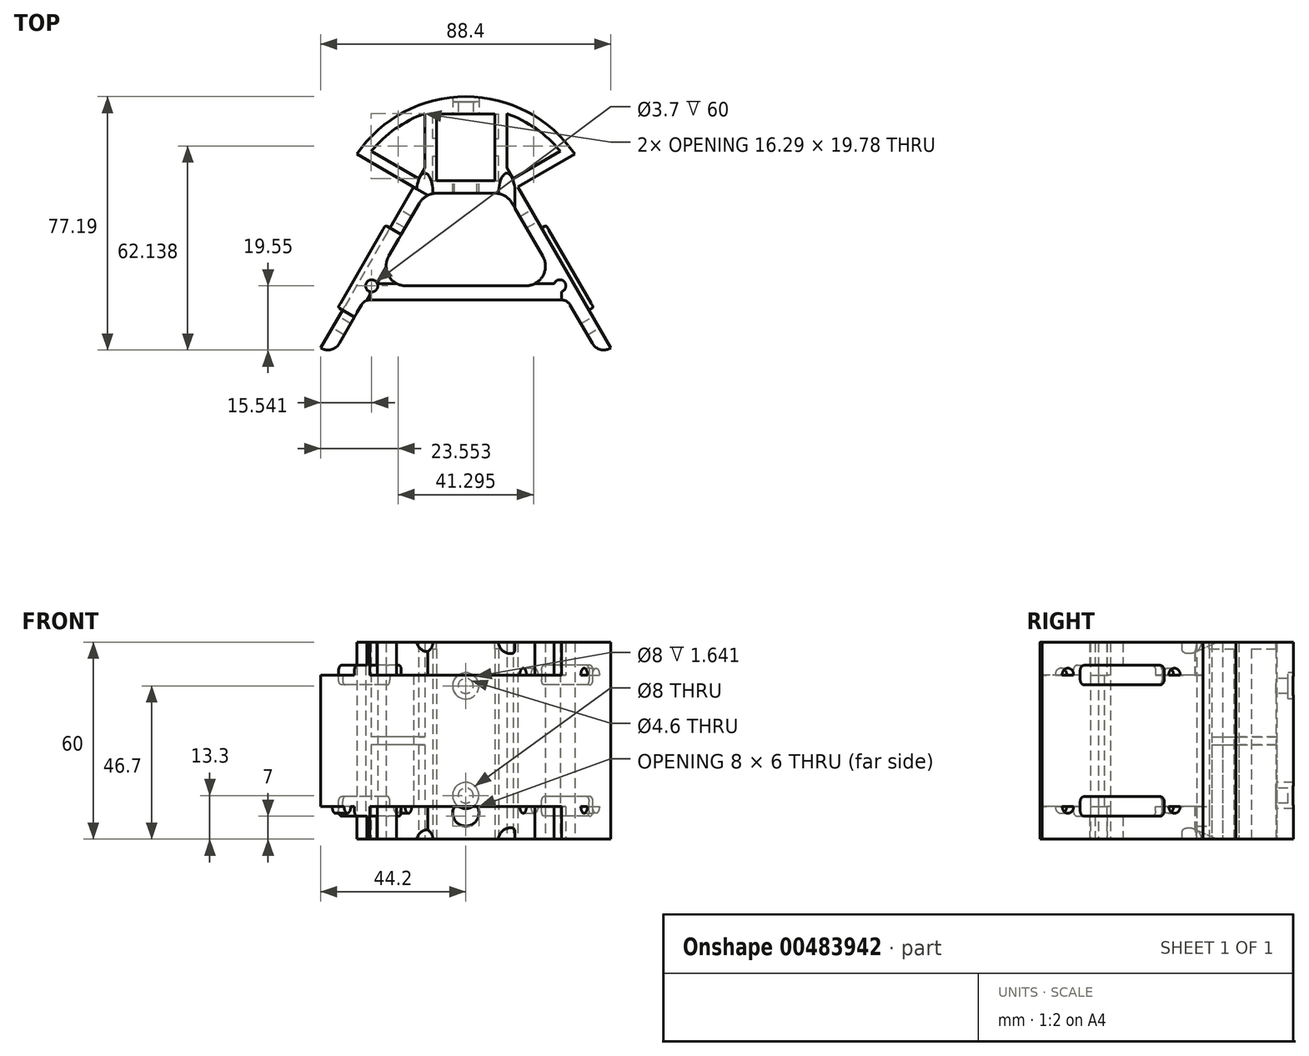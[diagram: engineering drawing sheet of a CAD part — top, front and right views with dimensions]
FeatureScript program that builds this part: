
annotation { "Feature Type Name" : "Feature", "Feature Type Description" : "" }
export const myFeature = defineFeature(function(context is Context, id is Id, definition is map)
    precondition{}
    {
        {
            var Q0;
            Q0=qCreatedBy(makeId("Top.planeOp"),FACE);
            var sketch = newSketch(context, id + "F0", { "sketchPlane" : qUnion([Q0])});
            skLineSegment(sketch, "E0", {"start": v(0, 0) * mm, "end": v(10, 0) * mm});
            skLineSegment(sketch, "E1", {"start": v(10, 0) * mm, "end": v(10, 7.5) * mm});
            skLineSegment(sketch, "E2", {"start": v(10, 7.5) * mm, "end": v(8.9, 7.5) * mm});
            skLineSegment(sketch, "E3", {"start": v(8.9, 7.5) * mm, "end": v(8.9, 12.8) * mm});
            skLineSegment(sketch, "E4", {"start": v(8.9, 12.8) * mm, "end": v(10, 12.8) * mm});
            skLineSegment(sketch, "E5", {"start": v(10, 12.8) * mm, "end": v(10, 20.3) * mm});
            skLineSegment(sketch, "E6", {"start": v(10, 20.3) * mm, "end": v(0, 20.3) * mm});
            skLineSegment(sketch, "E7", {"start": v(0, -3.8) * mm, "end": v(8.91, -3.8) * mm});
            skLineSegment(sketch, "E8", {"start": v(0, -32) * mm, "end": v(18.27, -32) * mm});
            skLineSegment(sketch, "E9", {"start": v(23.46, -23) * mm, "end": v(14.11, -6.8) * mm});
            skLineSegment(sketch, "E10", {"start": v(0, -36.3) * mm, "end": v(29.18, -36.3) * mm});
            skLineSegment(sketch, "E11", {"start": v(31.78, -37.8) * mm, "end": v(38.56, -49.55) * mm});
            skLineSegment(sketch, "E12", {"start": v(15.9, -1.9) * mm, "end": v(44.2, -50.92) * mm});
            skLineSegment(sketch, "E13", {"start": v(15.9, -1.9) * mm, "end": v(33.22, 8.1) * mm});
            skLineSegment(sketch, "E14", {"start": v(14.4, 0.7) * mm, "end": v(28.8, 9) * mm});
            skLineSegment(sketch, "E15", {"start": v(28.8, 9) * mm, "end": v(14.4, 0.7) * mm});
            skLineSegment(sketch, "E16", {"start": v(14.4, 0.7) * mm, "end": v(12.5, 3.99) * mm});
            skLineSegment(sketch, "E17", {"start": v(12.5, 3.99) * mm, "end": v(12.5, 20.48) * mm});
            skLineSegment(sketch, "E18", {"start": v(12.5, 3.99) * mm, "end": v(0, 25.64) * mm, "construction": true});
            skLineSegment(sketch, "E19", {"start": v(0, 25.64) * mm, "end": v(0, -14.6) * mm, "construction": true});
            skLineSegment(sketch, "E20", {"start": v(0, -14.6) * mm, "end": v(33.22, 8.1) * mm, "construction": true});
            skArc(sketch, "E21", {"start": v(0, 25.64) * mm, "mid": v(18.78, 20.99) * mm, "end": v(33.22, 8.1) * mm});
            skLineSegment(sketch, "E22", {"start": v(12.5, 20.48) * mm, "end": v(13.5, 23.3) * mm, "construction": true});
            skLineSegment(sketch, "E23", {"start": v(28.8, 9) * mm, "end": v(31.12, 10.91) * mm, "construction": true});
            skArc(sketch, "E24", {"start": v(28.8, 9) * mm, "mid": v(21.43, 15.85) * mm, "end": v(12.5, 20.48) * mm});
            skLineSegment(sketch, "E25", {"start": v(44.2, -50.92) * mm, "end": v(44.03, -51.02) * mm});
            skPoint(sketch, "E26.visualSharp", {"position": v(40.56, -53.02) * mm});
            skArc(sketch, "E26.filletArc", {"start": v(38.56, -49.55) * mm, "mid": v(41, -51.42) * mm, "end": v(44.03, -51.02) * mm});
            skPoint(sketch, "E27.visualSharp", {"position": v(30.91, -36.3) * mm});
            skArc(sketch, "E27.filletArc", {"start": v(31.78, -37.8) * mm, "mid": v(30.68, -36.7) * mm, "end": v(29.18, -36.3) * mm});
            skPoint(sketch, "E28.visualSharp", {"position": v(28.66, -32) * mm});
            skArc(sketch, "E28.filletArc", {"start": v(18.27, -32) * mm, "mid": v(23.46, -29) * mm, "end": v(23.46, -23) * mm});
            skPoint(sketch, "E29.visualSharp", {"position": v(12.38, -3.8) * mm});
            skArc(sketch, "E29.filletArc", {"start": v(14.11, -6.8) * mm, "mid": v(11.91, -4.6) * mm, "end": v(8.91, -3.8) * mm});
            skCircle(sketch, "E30", {"center": v(28.66, -32) * mm, "radius": 1.85 * mm});
            skLineSegment(sketch, "E31.MirrorCS", {"start": v(-44.2, -50.92) * mm, "end": v(-44.03, -51.02) * mm});
            skLineSegment(sketch, "E32.MirrorCS", {"start": v(-14.4, 0.7) * mm, "end": v(-12.5, 3.99) * mm});
            skLineSegment(sketch, "E33.MirrorCS", {"start": v(-10, 7.5) * mm, "end": v(-8.9, 7.5) * mm});
            skLineSegment(sketch, "E34.MirrorCS", {"start": v(-8.9, 12.8) * mm, "end": v(-10, 12.8) * mm});
            skLineSegment(sketch, "E35.MirrorCS", {"start": v(-28.8, 9) * mm, "end": v(-31.12, 10.91) * mm, "construction": true});
            skArc(sketch, "E36.MirrorCS", {"start": v(-31.78, -37.8) * mm, "mid": v(-30.68, -36.7) * mm, "end": v(-29.18, -36.3) * mm});
            skLineSegment(sketch, "E37.MirrorCS", {"start": v(-10, 0) * mm, "end": v(-10, 7.5) * mm});
            skArc(sketch, "E38.MirrorCS", {"start": v(-14.11, -6.8) * mm, "mid": v(-11.91, -4.6) * mm, "end": v(-8.91, -3.8) * mm});
            skLineSegment(sketch, "E39.MirrorCS", {"start": v(-12.5, 20.48) * mm, "end": v(-13.5, 23.3) * mm, "construction": true});
            skLineSegment(sketch, "E40.MirrorCS", {"start": v(-14.4, 0.7) * mm, "end": v(-28.8, 9) * mm});
            skLineSegment(sketch, "E41.MirrorCS", {"start": v(0, 0) * mm, "end": v(-10, 0) * mm});
            skArc(sketch, "E42.MirrorCS", {"start": v(-38.56, -49.55) * mm, "mid": v(-41, -51.42) * mm, "end": v(-44.03, -51.02) * mm});
            skCircle(sketch, "E43.MirrorC", {"center": v(-28.66, -32) * mm, "radius": 1.85 * mm});
            skLineSegment(sketch, "E44.MirrorCS", {"start": v(-8.9, 7.5) * mm, "end": v(-8.9, 12.8) * mm});
            skLineSegment(sketch, "E45.MirrorCS", {"start": v(-10, 12.8) * mm, "end": v(-10, 20.3) * mm});
            skLineSegment(sketch, "E46.MirrorCS", {"start": v(-12.5, 3.99) * mm, "end": v(0, 25.64) * mm, "construction": true});
            skLineSegment(sketch, "E47.MirrorCS", {"start": v(0, -14.6) * mm, "end": v(-33.22, 8.1) * mm, "construction": true});
            skPoint(sketch, "E48.MirrorP", {"position": v(-40.56, -53.02) * mm});
            skLineSegment(sketch, "E49.MirrorCS", {"start": v(-15.9, -1.9) * mm, "end": v(-44.2, -50.92) * mm});
            skLineSegment(sketch, "E50.MirrorCS", {"start": v(-31.78, -37.8) * mm, "end": v(-38.56, -49.55) * mm});
            skLineSegment(sketch, "E51.MirrorCS", {"start": v(-28.8, 9) * mm, "end": v(-14.4, 0.7) * mm});
            skLineSegment(sketch, "E52.MirrorCS", {"start": v(0, -36.3) * mm, "end": v(-29.18, -36.3) * mm});
            skLineSegment(sketch, "E53.MirrorCS", {"start": v(-23.46, -23) * mm, "end": v(-14.11, -6.8) * mm});
            skLineSegment(sketch, "E54.MirrorCS", {"start": v(-12.5, 3.99) * mm, "end": v(-12.5, 20.48) * mm});
            skLineSegment(sketch, "E55.MirrorCS", {"start": v(-15.9, -1.9) * mm, "end": v(-33.22, 8.1) * mm});
            skArc(sketch, "E56.MirrorCS", {"start": v(-18.27, -32) * mm, "mid": v(-23.46, -29) * mm, "end": v(-23.46, -23) * mm});
            skLineSegment(sketch, "E57.MirrorCS", {"start": v(0, -32) * mm, "end": v(-18.27, -32) * mm});
            skArc(sketch, "E58.MirrorCS", {"start": v(-28.8, 9) * mm, "mid": v(-21.43, 15.85) * mm, "end": v(-12.5, 20.48) * mm});
            skPoint(sketch, "E59.MirrorP", {"position": v(-12.38, -3.8) * mm});
            skLineSegment(sketch, "E60.MirrorCS", {"start": v(0, -3.8) * mm, "end": v(-8.91, -3.8) * mm});
            skLineSegment(sketch, "E61.MirrorCS", {"start": v(-10, 20.3) * mm, "end": v(0, 20.3) * mm});
            skPoint(sketch, "E62.MirrorP", {"position": v(-30.91, -36.3) * mm});
            skArc(sketch, "E63.MirrorCS", {"start": v(0, 25.64) * mm, "mid": v(-18.78, 20.99) * mm, "end": v(-33.22, 8.1) * mm});
            skSolve(sketch);
        }
        {
            var Q0;
            Q0=makeQuery(id+"F0.imprint","IMPRINT",FACE,{"disambiguationData":[TD([[makeQuery(id+"F0.imprint","IMPRINT",EDGE,{"derivedFrom":sQuery(id+"F0.wireOp",EDGE,"E0")}),-1.0]])]});
            extrude(context, id + "F1", {"entities" : qUnion([Q0]), "depth" : 30 * mm, "hasSecondDirection" : true, "secondDirectionOppositeDirection" : true, "secondDirectionDepth" : 30 * mm});
        }
        {
            var Q0;
            Q0=makeQuery(id+"F0.imprint","IMPRINT",FACE,{"disambiguationData":[TD([[makeQuery(id+"F0.imprint","IMPRINT",EDGE,{"derivedFrom":sQuery(id+"F0.wireOp",EDGE,"E32.MirrorCS")}),1.0]])]});
            var Q1;
            Q1=makeQuery(id+"F0.imprint","IMPRINT",FACE,{"disambiguationData":[TD([[makeQuery(id+"F0.imprint","IMPRINT",EDGE,{"derivedFrom":sQuery(id+"F0.wireOp",EDGE,"E15")}),-1.0]])]});
            extrude(context, id + "F2", {"entities" : qUnion([Q0, Q1]), "operationType" : NewBodyOperationType.ADD, "depth" : 1.2 * mm, "hasSecondDirection" : true, "secondDirectionOppositeDirection" : true, "secondDirectionDepth" : 1.2 * mm});
        }
        {
            var Q0;
            Q0=makeQuery(id+"F1.opExtrude","SWEPT_FACE",FACE,{"disambiguationData":[OSD([sQuery(id+"F0.wireOp",EDGE,"E0"),sQuery(id+"F0.wireOp",EDGE,"E41.MirrorCS")])]});
            var sketch = newSketch(context, id + "F3", { "sketchPlane" : qUnion([Q0])});
            skCircle(sketch, "E64", {"center": v(0, 0) * mm, "radius": 7 * mm});
            skCircle(sketch, "E65", {"center": v(0, -22) * mm, "radius": 4 * mm});
            skSolve(sketch);
        }
        {
            var Q0;
            Q0=makeQuery(id+"F3.imprint","IMPRINT",FACE,{"disambiguationData":[TD([[makeQuery(id+"F3.imprint","IMPRINT",EDGE,{"derivedFrom":sQuery(id+"F3.wireOp",EDGE,"E64")}),1.0]])]});
            var Q1;
            Q1=makeQuery(id+"F3.imprint","IMPRINT",FACE,{"disambiguationData":[TD([[makeQuery(id+"F3.imprint","IMPRINT",EDGE,{"derivedFrom":sQuery(id+"F3.wireOp",EDGE,"E65")}),1.0]])]});
            extrude(context, id + "F4", {"entities" : qUnion([Q0, Q1]), "operationType" : NewBodyOperationType.REMOVE, "oppositeDirection" : true, "depth" : 5 * mm});
        }
        {
            var Q0;
            Q0=makeQuery(id+"F1.opExtrude","SWEPT_FACE",FACE,{"disambiguationData":[OSD([sQuery(id+"F0.wireOp",EDGE,"E10"),sQuery(id+"F0.wireOp",EDGE,"E52.MirrorCS")])]});
            var sketch = newSketch(context, id + "F5", { "sketchPlane" : qUnion([Q0])});
            skCircle(sketch, "E66", {"center": v(0, 0) * mm, "radius": 11.8 * mm});
            skCircle(sketch, "E67", {"center": v(0, -22.5) * mm, "radius": 4.5 * mm});
            skCircle(sketch, "E68", {"center": v(15.4, 15.4) * mm, "radius": 1.6 * mm});
            skCircle(sketch, "E69.MirrorC", {"center": v(-15.4, 15.4) * mm, "radius": 1.6 * mm});
            skCircle(sketch, "E70.MirrorC", {"center": v(-15.4, -15.4) * mm, "radius": 1.6 * mm});
            skCircle(sketch, "E71.MirrorC", {"center": v(15.4, -15.4) * mm, "radius": 1.6 * mm});
            skSolve(sketch);
        }
        {
            var Q0;
            Q0=makeQuery(id+"F5.imprint","IMPRINT",FACE,{"disambiguationData":[TD([[makeQuery(id+"F5.imprint","IMPRINT",EDGE,{"derivedFrom":sQuery(id+"F5.wireOp",EDGE,"E66")}),1.0]])]});
            var Q1;
            Q1=makeQuery(id+"F5.imprint","IMPRINT",FACE,{"disambiguationData":[TD([[makeQuery(id+"F5.imprint","IMPRINT",EDGE,{"derivedFrom":sQuery(id+"F5.wireOp",EDGE,"E67")}),1.0]])]});
            var Q2;
            Q2=makeQuery(id+"F5.imprint","IMPRINT",FACE,{"disambiguationData":[TD([[makeQuery(id+"F5.imprint","IMPRINT",EDGE,{"derivedFrom":sQuery(id+"F5.wireOp",EDGE,"E71.MirrorC")}),-1.0]])]});
            var Q3;
            Q3=makeQuery(id+"F5.imprint","IMPRINT",FACE,{"disambiguationData":[TD([[makeQuery(id+"F5.imprint","IMPRINT",EDGE,{"derivedFrom":sQuery(id+"F5.wireOp",EDGE,"E68")}),1.0]])]});
            var Q4;
            Q4=makeQuery(id+"F5.imprint","IMPRINT",FACE,{"disambiguationData":[TD([[makeQuery(id+"F5.imprint","IMPRINT",EDGE,{"derivedFrom":sQuery(id+"F5.wireOp",EDGE,"E69.MirrorC")}),-1.0]])]});
            var Q5;
            Q5=makeQuery(id+"F5.imprint","IMPRINT",FACE,{"disambiguationData":[TD([[makeQuery(id+"F5.imprint","IMPRINT",EDGE,{"derivedFrom":sQuery(id+"F5.wireOp",EDGE,"E70.MirrorC")}),1.0]])]});
            extrude(context, id + "F6", {"entities" : qUnion([Q0, Q1, Q2, Q3, Q4, Q5]), "operationType" : NewBodyOperationType.REMOVE, "oppositeDirection" : true, "depth" : 5 * mm});
        }
        {
            var Q0;
            Q0=makeQuery(id+"F1.opExtrude","SWEPT_FACE",FACE,{"disambiguationData":[OSD([sQuery(id+"F0.wireOp",EDGE,"E12")])]});
            var sketch = newSketch(context, id + "F7", { "sketchPlane" : qUnion([Q0])});
            skCircle(sketch, "E72", {"center": v(-23.85, 0) * mm, "radius": 12.75 * mm});
            skLineSegment(sketch, "E73", {"start": v(-59.2, 7.25) * mm, "end": v(-59.2, -7.25) * mm});
            skLineSegment(sketch, "E74", {"start": v(-53.5, 7.25) * mm, "end": v(-53.5, -7.25) * mm});
            skArc(sketch, "E75", {"start": v(-53.5, 7.25) * mm, "mid": v(-56.35, 10.1) * mm, "end": v(-59.2, 7.25) * mm});
            skArc(sketch, "E76", {"start": v(-59.2, -7.25) * mm, "mid": v(-56.35, -10.1) * mm, "end": v(-53.5, -7.25) * mm});
            skCircle(sketch, "E77", {"center": v(-57.2, 20.1) * mm, "radius": 2 * mm});
            skPoint(sketch, "E77.centerSnap0", {"position": v(-56.35, 10.1) * mm});
            skCircle(sketch, "E78", {"center": v(-57.2, -20.1) * mm, "radius": 2 * mm});
            skCircle(sketch, "E79", {"center": v(-19.7, 20.1) * mm, "radius": 2 * mm});
            skCircle(sketch, "E80", {"center": v(-19.7, -20.1) * mm, "radius": 2 * mm});
            skLineSegment(sketch, "E81.bottom", {"start": v(-52.85, 23) * mm, "end": v(-24.05, 23) * mm});
            skLineSegment(sketch, "E81.top", {"start": v(-52.85, 17) * mm, "end": v(-24.05, 17) * mm});
            skLineSegment(sketch, "E81.left", {"start": v(-52.85, 23) * mm, "end": v(-52.85, 17) * mm});
            skLineSegment(sketch, "E81.right", {"start": v(-24.05, 23) * mm, "end": v(-24.05, 17) * mm});
            skLineSegment(sketch, "E82.MirrorCS", {"start": v(-52.85, -17) * mm, "end": v(-24.05, -17) * mm});
            skLineSegment(sketch, "E83.MirrorCS", {"start": v(-52.85, -23) * mm, "end": v(-52.85, -17) * mm});
            skLineSegment(sketch, "E84.MirrorCS", {"start": v(-52.85, -23) * mm, "end": v(-24.05, -23) * mm});
            skLineSegment(sketch, "E85.MirrorCS", {"start": v(-24.05, -23) * mm, "end": v(-24.05, -17) * mm});
            skSolve(sketch);
        }
        {
            var Q0;
            Q0=makeQuery(id+"F7.imprint","IMPRINT",FACE,{"disambiguationData":[TD([[makeQuery(id+"F7.imprint","IMPRINT",EDGE,{"derivedFrom":sQuery(id+"F7.wireOp",EDGE,"E73")}),1.0]])]});
            var Q1;
            Q1=makeQuery(id+"F7.imprint","IMPRINT",FACE,{"disambiguationData":[TD([[makeQuery(id+"F7.imprint","IMPRINT",EDGE,{"derivedFrom":sQuery(id+"F7.wireOp",EDGE,"E72")}),1.0]])]});
            var Q2;
            Q2=makeQuery(id+"F7.imprint","IMPRINT",FACE,{"disambiguationData":[TD([[makeQuery(id+"F7.imprint","IMPRINT",EDGE,{"derivedFrom":sQuery(id+"F7.wireOp",EDGE,"E79")}),1.0]])]});
            var Q3;
            Q3=makeQuery(id+"F7.imprint","IMPRINT",FACE,{"disambiguationData":[TD([[makeQuery(id+"F7.imprint","IMPRINT",EDGE,{"derivedFrom":sQuery(id+"F7.wireOp",EDGE,"E77")}),1.0]])]});
            var Q4;
            Q4=makeQuery(id+"F7.imprint","IMPRINT",FACE,{"disambiguationData":[TD([[makeQuery(id+"F7.imprint","IMPRINT",EDGE,{"derivedFrom":sQuery(id+"F7.wireOp",EDGE,"E78")}),1.0]])]});
            var Q5;
            Q5=makeQuery(id+"F7.imprint","IMPRINT",FACE,{"disambiguationData":[TD([[makeQuery(id+"F7.imprint","IMPRINT",EDGE,{"derivedFrom":sQuery(id+"F7.wireOp",EDGE,"E80")}),1.0]])]});
            extrude(context, id + "F8", {"entities" : qUnion([Q0, Q1, Q2, Q3, Q4, Q5]), "operationType" : NewBodyOperationType.REMOVE, "oppositeDirection" : true, "depth" : 5 * mm});
        }
        {
            var Q0;
            Q0=makeQuery(id+"F7.imprint","IMPRINT",FACE,{"disambiguationData":[TD([[makeQuery(id+"F7.imprint","IMPRINT",EDGE,{"derivedFrom":sQuery(id+"F7.wireOp",EDGE,"E81.bottom")}),-1.0]])]});
            var Q1;
            Q1=makeQuery(id+"F7.imprint","IMPRINT",FACE,{"disambiguationData":[TD([[makeQuery(id+"F7.imprint","IMPRINT",EDGE,{"derivedFrom":sQuery(id+"F7.wireOp",EDGE,"E82.MirrorCS")}),-1.0]])]});
            extrude(context, id + "F9", {"entities" : qUnion([Q0, Q1]), "operationType" : NewBodyOperationType.ADD, "depth" : 1.6 * mm});
        }
        {
            var Q0;
            Q0=makeQuery(id+"F1.opExtrude","SWEPT_FACE",FACE,{"disambiguationData":[OSD([sQuery(id+"F0.wireOp",EDGE,"E49.MirrorCS")])]});
            var sketch = newSketch(context, id + "F10", { "sketchPlane" : qUnion([Q0])});
            skCircle(sketch, "E86", {"center": v(23.85, 0) * mm, "radius": 12.75 * mm});
            skLineSegment(sketch, "E87", {"start": v(53.5, 7.25) * mm, "end": v(53.5, -7.25) * mm});
            skLineSegment(sketch, "E88", {"start": v(59.2, 7.25) * mm, "end": v(59.2, -7.25) * mm});
            skArc(sketch, "E89", {"start": v(59.2, 7.25) * mm, "mid": v(56.35, 10.1) * mm, "end": v(53.5, 7.25) * mm});
            skArc(sketch, "E90", {"start": v(53.5, -7.25) * mm, "mid": v(56.35, -10.1) * mm, "end": v(59.2, -7.25) * mm});
            skCircle(sketch, "E91", {"center": v(19.7, 20.1) * mm, "radius": 2 * mm});
            skPoint(sketch, "E91.centerSnap0", {"position": v(56.35, 10.1) * mm});
            skCircle(sketch, "E92", {"center": v(57.2, 20.1) * mm, "radius": 2 * mm});
            skLineSegment(sketch, "E93.bottom", {"start": v(24.05, 23) * mm, "end": v(52.85, 23) * mm});
            skLineSegment(sketch, "E93.top", {"start": v(24.05, 17) * mm, "end": v(52.85, 17) * mm});
            skLineSegment(sketch, "E93.left", {"start": v(24.05, 23) * mm, "end": v(24.05, 17) * mm});
            skLineSegment(sketch, "E93.right", {"start": v(52.85, 23) * mm, "end": v(52.85, 17) * mm});
            skLineSegment(sketch, "E94.MirrorCS", {"start": v(24.05, -23) * mm, "end": v(52.85, -23) * mm});
            skLineSegment(sketch, "E95.MirrorCS", {"start": v(52.85, -23) * mm, "end": v(52.85, -17) * mm});
            skLineSegment(sketch, "E96.MirrorCS", {"start": v(24.05, -23) * mm, "end": v(24.05, -17) * mm});
            skLineSegment(sketch, "E97.MirrorCS", {"start": v(24.05, -17) * mm, "end": v(52.85, -17) * mm});
            skCircle(sketch, "E98.MirrorC", {"center": v(57.2, -20.1) * mm, "radius": 2 * mm});
            skCircle(sketch, "E99.MirrorC", {"center": v(19.7, -20.1) * mm, "radius": 2 * mm});
            skSolve(sketch);
        }
        {
            var Q0;
            Q0=makeQuery(id+"F10.imprint","IMPRINT",FACE,{"disambiguationData":[TD([[makeQuery(id+"F10.imprint","IMPRINT",EDGE,{"derivedFrom":sQuery(id+"F10.wireOp",EDGE,"E86")}),1.0]])]});
            var Q1;
            Q1=makeQuery(id+"F10.imprint","IMPRINT",FACE,{"disambiguationData":[TD([[makeQuery(id+"F10.imprint","IMPRINT",EDGE,{"derivedFrom":sQuery(id+"F10.wireOp",EDGE,"E87")}),1.0]])]});
            var Q2;
            Q2=makeQuery(id+"F10.imprint","IMPRINT",FACE,{"disambiguationData":[TD([[makeQuery(id+"F10.imprint","IMPRINT",EDGE,{"derivedFrom":sQuery(id+"F10.wireOp",EDGE,"E98.MirrorC")}),-1.0]])]});
            var Q3;
            Q3=makeQuery(id+"F10.imprint","IMPRINT",FACE,{"disambiguationData":[TD([[makeQuery(id+"F10.imprint","IMPRINT",EDGE,{"derivedFrom":sQuery(id+"F10.wireOp",EDGE,"E91")}),1.0]])]});
            var Q4;
            Q4=makeQuery(id+"F10.imprint","IMPRINT",FACE,{"disambiguationData":[TD([[makeQuery(id+"F10.imprint","IMPRINT",EDGE,{"derivedFrom":sQuery(id+"F10.wireOp",EDGE,"E92")}),1.0]])]});
            var Q5;
            Q5=makeQuery(id+"F10.imprint","IMPRINT",FACE,{"disambiguationData":[TD([[makeQuery(id+"F10.imprint","IMPRINT",EDGE,{"derivedFrom":sQuery(id+"F10.wireOp",EDGE,"E99.MirrorC")}),-1.0]])]});
            extrude(context, id + "F11", {"entities" : qUnion([Q0, Q1, Q2, Q3, Q4, Q5]), "operationType" : NewBodyOperationType.REMOVE, "oppositeDirection" : true, "depth" : 5 * mm});
        }
        {
            var Q0;
            Q0=makeQuery(id+"F10.imprint","IMPRINT",FACE,{"disambiguationData":[TD([[makeQuery(id+"F10.imprint","IMPRINT",EDGE,{"derivedFrom":sQuery(id+"F10.wireOp",EDGE,"E93.bottom")}),-1.0]])]});
            var Q1;
            Q1=makeQuery(id+"F10.imprint","IMPRINT",FACE,{"disambiguationData":[TD([[makeQuery(id+"F10.imprint","IMPRINT",EDGE,{"derivedFrom":sQuery(id+"F10.wireOp",EDGE,"E94.MirrorCS")}),1.0]])]});
            extrude(context, id + "F12", {"entities" : qUnion([Q0, Q1]), "operationType" : NewBodyOperationType.ADD, "depth" : 1.6 * mm});
        }
        {
            var Q0;
            Q0=makeQuery(id+"F0.imprint","IMPRINT",FACE,{"disambiguationData":[TD([[makeQuery(id+"F0.imprint","IMPRINT",EDGE,{"derivedFrom":sQuery(id+"F0.wireOp",EDGE,"E43.MirrorC")}),-1.0]])]});
            var Q1;
            Q1=makeQuery(id+"F0.imprint","IMPRINT",FACE,{"disambiguationData":[TD([[makeQuery(id+"F0.imprint","IMPRINT",EDGE,{"derivedFrom":sQuery(id+"F0.wireOp",EDGE,"E30")}),1.0]])]});
            extrude(context, id + "F13", {"entities" : qUnion([Q0, Q1]), "operationType" : NewBodyOperationType.ADD, "depth" : 20 * mm, "hasSecondDirection" : true, "secondDirectionOppositeDirection" : true, "secondDirectionDepth" : 20 * mm});
        }
        {
            var Q0;
            Q0=makeQuery(id+"F1.opExtrude","SWEPT_FACE",FACE,{"disambiguationData":[OSD([sQuery(id+"F0.wireOp",EDGE,"E6"),sQuery(id+"F0.wireOp",EDGE,"E61.MirrorCS")])]});
            var sketch = newSketch(context, id + "F14", { "sketchPlane" : qUnion([Q0])});
            skCircle(sketch, "E100", {"center": v(0, 16.7) * mm, "radius": 2.3 * mm});
            skCircle(sketch, "E101.MirrorC", {"center": v(0, -16.7) * mm, "radius": 2.3 * mm});
            skCircle(sketch, "E102", {"center": v(0, -16.7) * mm, "radius": 4 * mm});
            skCircle(sketch, "E103", {"center": v(0, 16.7) * mm, "radius": 4 * mm});
            skSolve(sketch);
        }
        {
            var Q0;
            Q0=makeQuery(id+"F14.imprint","IMPRINT",FACE,{"disambiguationData":[TD([[makeQuery(id+"F14.imprint","IMPRINT",EDGE,{"derivedFrom":sQuery(id+"F14.wireOp",EDGE,"E101.MirrorC")}),-1.0]])]});
            var Q1;
            Q1=makeQuery(id+"F14.imprint","IMPRINT",FACE,{"disambiguationData":[TD([[makeQuery(id+"F14.imprint","IMPRINT",EDGE,{"derivedFrom":sQuery(id+"F14.wireOp",EDGE,"E100")}),1.0]])]});
            extrude(context, id + "F15", {"entities" : qUnion([Q0, Q1]), "operationType" : NewBodyOperationType.REMOVE, "oppositeDirection" : true, "depth" : 8 * mm});
        }
        {
            var Q0;
            Q0=makeQuery(id+"F14.imprint","IMPRINT",FACE,{"disambiguationData":[TD([[makeQuery(id+"F14.imprint","IMPRINT",EDGE,{"derivedFrom":sQuery(id+"F14.wireOp",EDGE,"E101.MirrorC")}),1.0]])]});
            var Q1;
            Q1=makeQuery(id+"F14.imprint","IMPRINT",FACE,{"disambiguationData":[TD([[makeQuery(id+"F14.imprint","IMPRINT",EDGE,{"derivedFrom":sQuery(id+"F14.wireOp",EDGE,"E100")}),-1.0]])]});
            extrude(context, id + "F16", {"entities" : qUnion([Q0, Q1]), "operationType" : NewBodyOperationType.REMOVE, "oppositeDirection" : true, "depth" : 6 * mm});
        }
        {
            var Q0;
            Q0=makeQuery(id+"F14.imprint","IMPRINT",FACE,{"disambiguationData":[TD([[makeQuery(id+"F14.imprint","IMPRINT",EDGE,{"derivedFrom":sQuery(id+"F14.wireOp",EDGE,"E101.MirrorC")}),1.0]])]});
            var Q1;
            Q1=makeQuery(id+"F14.imprint","IMPRINT",FACE,{"disambiguationData":[TD([[makeQuery(id+"F14.imprint","IMPRINT",EDGE,{"derivedFrom":sQuery(id+"F14.wireOp",EDGE,"E100")}),-1.0]])]});
            extrude(context, id + "F17", {"entities" : qUnion([Q0, Q1]), "operationType" : NewBodyOperationType.ADD, "oppositeDirection" : true, "depth" : 3.7 * mm});
        }
        {
            var Q0;
            Q0=makeQuery(id+"F1.opExtrude","CAP_EDGE",EDGE,{"disambiguationData":[OSD([sQuery(id+"F0.wireOp",EDGE,"E7"),sQuery(id+"F0.wireOp",EDGE,"E60.MirrorCS")])],"isStart":true});
            cPoint(context, id + "F18", {"entities" : qUnion([Q0]), "parameter" : 0.5});
        }
        {
            var Q0;
            Q0=sQuery(id+"F5.wireOp",VERTEX,"E71.MirrorC.center");
            var Q1;
            Q1=sQuery(id+"F5.wireOp",VERTEX,"E70.MirrorC.center");
            var Q2;
            Q2 = qCreatedBy(id + "F18" ,VERTEX);
            cPlane(context, id + "F19", {"entities" : qUnion([Q0, Q1, Q2]), "cplaneType" : CPlaneType.THREE_POINT, "offset" : 25 * mm, "flipAlignment" : true, "width" : 150 * mm, "height" : 150 * mm});
        }
        {
            var Q0;
            Q0=qCreatedBy(id+"F19.planeOp",FACE);
            var sketch = newSketch(context, id + "F20", { "sketchPlane" : qUnion([Q0])});
            skLineSegment(sketch, "E104.bottom", {"start": v(-8.91, 8.83) * mm, "end": v(8.91, 8.83) * mm});
            skLineSegment(sketch, "E104.top", {"start": v(-8.91, 3.83) * mm, "end": v(8.91, 3.83) * mm});
            skLineSegment(sketch, "E104.left", {"start": v(-8.91, 8.83) * mm, "end": v(-8.91, 3.83) * mm});
            skLineSegment(sketch, "E104.right", {"start": v(8.91, 8.83) * mm, "end": v(8.91, 3.83) * mm});
            skSolve(sketch);
        }
        {
            var Q0;
            Q0=makeQuery(id+"F20.imprint","IMPRINT",FACE,{"disambiguationData":[TD([[makeQuery(id+"F20.imprint","IMPRINT",EDGE,{"derivedFrom":sQuery(id+"F20.wireOp",EDGE,"E104.bottom")}),-1.0]])]});
            extrude(context, id + "F21", {"entities" : qUnion([Q0]), "oppositeDirection" : true, "depth" : 20 * mm});
        }
        {
            var Q0;
            Q0=makeQuery(id+"F21.opExtrude","SWEPT_FACE",FACE,{"disambiguationData":[OSD([sQuery(id+"F20.wireOp",EDGE,"E104.bottom")])]});
            var sketch = newSketch(context, id + "F22", { "sketchPlane" : qUnion([Q0])});
            skCircle(sketch, "E105", {"center": v(-12.5, -28.92) * mm, "radius": 2.5 * mm});
            skCircle(sketch, "E106", {"center": v(12.5, -28.92) * mm, "radius": 2.5 * mm});
            skLineSegment(sketch, "E107.bottom", {"start": v(15, -28.92) * mm, "end": v(10, -28.92) * mm});
            skLineSegment(sketch, "E107.top", {"start": v(15, -35.42) * mm, "end": v(10, -35.42) * mm});
            skLineSegment(sketch, "E107.left", {"start": v(15, -28.92) * mm, "end": v(15, -35.42) * mm});
            skLineSegment(sketch, "E107.right", {"start": v(10, -28.92) * mm, "end": v(10, -35.42) * mm});
            skLineSegment(sketch, "E108.bottom", {"start": v(-15, -28.92) * mm, "end": v(-10, -28.92) * mm});
            skLineSegment(sketch, "E108.top", {"start": v(-15, -35.42) * mm, "end": v(-10, -35.42) * mm});
            skLineSegment(sketch, "E108.left", {"start": v(-15, -28.92) * mm, "end": v(-15, -35.42) * mm});
            skLineSegment(sketch, "E108.right", {"start": v(-10, -28.92) * mm, "end": v(-10, -35.42) * mm});
            skSolve(sketch);
        }
        {
            var Q0;
            {var subQ0=sQuery(id+"F22.wireOp",EDGE,"E107.bottom");Q0=makeQuery(id+"F22.imprint","IMPRINT",FACE,{"disambiguationData":[TD([[makeQuery(id+"F22.imprint","IMPRINT",EDGE,{"derivedFrom":subQ0}),1.0]])]});}
            var Q1;
            Q1=makeQuery(id+"F22.imprint","IMPRINT",FACE,{"disambiguationData":[TD([[makeQuery(id+"F22.imprint","IMPRINT",EDGE,{"derivedFrom":sQuery(id+"F22.wireOp",EDGE,"E107.top")}),-1.0]])]});
            var Q2;
            Q2=makeQuery(id+"F22.imprint","IMPRINT",FACE,{"disambiguationData":[TD([[makeQuery(id+"F22.imprint","IMPRINT",EDGE,{"derivedFrom":sQuery(id+"F22.wireOp",EDGE,"E108.top")}),1.0]])]});
            var Q3;
            {var subQ0=sQuery(id+"F22.wireOp",EDGE,"E108.bottom");Q3=makeQuery(id+"F22.imprint","IMPRINT",FACE,{"disambiguationData":[TD([[makeQuery(id+"F22.imprint","IMPRINT",EDGE,{"derivedFrom":subQ0}),-1.0]])]});}
            var Q4;
            {var subQ0=sQuery(id+"F22.wireOp",EDGE,"E107.bottom");Q4=makeQuery(id+"F22.imprint","IMPRINT",FACE,{"disambiguationData":[TD([[makeQuery(id+"F22.imprint","IMPRINT",EDGE,{"derivedFrom":subQ0}),-1.0]])]});}
            var Q5;
            {var subQ0=sQuery(id+"F22.wireOp",EDGE,"E108.bottom");Q5=makeQuery(id+"F22.imprint","IMPRINT",FACE,{"disambiguationData":[TD([[makeQuery(id+"F22.imprint","IMPRINT",EDGE,{"derivedFrom":subQ0}),1.0]])]});}
            extrude(context, id + "F23", {"entities" : qUnion([Q0, Q1, Q2, Q3, Q4, Q5]), "oppositeDirection" : true, "depth" : 10 * mm, "hasSecondDirection" : true, "secondDirectionOppositeDirection" : false, "secondDirectionDepth" : 10 * mm});
        }
        {
            var Q0;
            Q0=makeQuery(id+"F1.opExtrude","CAP_FACE",FACE,{"disambiguationData":[OSD([sQuery(id+"F0.wireOp",EDGE,"E0"),sQuery(id+"F0.wireOp",EDGE,"E1"),sQuery(id+"F0.wireOp",EDGE,"E2"),sQuery(id+"F0.wireOp",EDGE,"E3"),sQuery(id+"F0.wireOp",EDGE,"E4"),sQuery(id+"F0.wireOp",EDGE,"E5"),sQuery(id+"F0.wireOp",EDGE,"E6"),sQuery(id+"F0.wireOp",EDGE,"E7"),sQuery(id+"F0.wireOp",EDGE,"E8"),sQuery(id+"F0.wireOp",EDGE,"E9"),sQuery(id+"F0.wireOp",EDGE,"E10"),sQuery(id+"F0.wireOp",EDGE,"E11"),sQuery(id+"F0.wireOp",EDGE,"E12"),sQuery(id+"F0.wireOp",EDGE,"E13"),sQuery(id+"F0.wireOp",EDGE,"E15"),sQuery(id+"F0.wireOp",EDGE,"E16"),sQuery(id+"F0.wireOp",EDGE,"E17"),sQuery(id+"F0.wireOp",EDGE,"E21"),sQuery(id+"F0.wireOp",EDGE,"E24"),sQuery(id+"F0.wireOp",EDGE,"E25"),sQuery(id+"F0.wireOp",EDGE,"E26.filletArc"),sQuery(id+"F0.wireOp",EDGE,"E27.filletArc"),sQuery(id+"F0.wireOp",EDGE,"E28.filletArc"),sQuery(id+"F0.wireOp",EDGE,"E29.filletArc"),sQuery(id+"F0.wireOp",EDGE,"E30"),sQuery(id+"F0.wireOp",EDGE,"E31.MirrorCS"),sQuery(id+"F0.wireOp",EDGE,"E32.MirrorCS"),sQuery(id+"F0.wireOp",EDGE,"E33.MirrorCS"),sQuery(id+"F0.wireOp",EDGE,"E34.MirrorCS"),sQuery(id+"F0.wireOp",EDGE,"E36.MirrorCS"),sQuery(id+"F0.wireOp",EDGE,"E37.MirrorCS"),sQuery(id+"F0.wireOp",EDGE,"E38.MirrorCS"),sQuery(id+"F0.wireOp",EDGE,"E41.MirrorCS"),sQuery(id+"F0.wireOp",EDGE,"E42.MirrorCS"),sQuery(id+"F0.wireOp",EDGE,"E43.MirrorC"),sQuery(id+"F0.wireOp",EDGE,"E44.MirrorCS"),sQuery(id+"F0.wireOp",EDGE,"E45.MirrorCS"),sQuery(id+"F0.wireOp",EDGE,"E49.MirrorCS"),sQuery(id+"F0.wireOp",EDGE,"E50.MirrorCS"),sQuery(id+"F0.wireOp",EDGE,"E51.MirrorCS"),sQuery(id+"F0.wireOp",EDGE,"E52.MirrorCS"),sQuery(id+"F0.wireOp",EDGE,"E53.MirrorCS"),sQuery(id+"F0.wireOp",EDGE,"E54.MirrorCS"),sQuery(id+"F0.wireOp",EDGE,"E55.MirrorCS"),sQuery(id+"F0.wireOp",EDGE,"E56.MirrorCS"),sQuery(id+"F0.wireOp",EDGE,"E57.MirrorCS"),sQuery(id+"F0.wireOp",EDGE,"E58.MirrorCS"),sQuery(id+"F0.wireOp",EDGE,"E60.MirrorCS"),sQuery(id+"F0.wireOp",EDGE,"E61.MirrorCS"),sQuery(id+"F0.wireOp",EDGE,"E63.MirrorCS")])],"isStart":false});
            var sketch = newSketch(context, id + "F24", { "sketchPlane" : qUnion([Q0])});
            skLineSegment(sketch, "E109", {"start": v(-8.9, 12.8) * mm, "end": v(-8.9, 20.3) * mm});
            skLineSegment(sketch, "E110", {"start": v(-8.9, 20.3) * mm, "end": v(-10, 20.3) * mm});
            skLineSegment(sketch, "E111", {"start": v(-10, 20.3) * mm, "end": v(-10, 0) * mm});
            skLineSegment(sketch, "E112", {"start": v(-10, 0) * mm, "end": v(-8.9, 0) * mm});
            skLineSegment(sketch, "E113", {"start": v(-8.9, 0) * mm, "end": v(-8.9, 12.8) * mm});
            skLineSegment(sketch, "E114", {"start": v(10, 20.3) * mm, "end": v(10, 0) * mm});
            skLineSegment(sketch, "E115", {"start": v(10, 0) * mm, "end": v(8.9, 0) * mm});
            skLineSegment(sketch, "E116", {"start": v(8.9, 0) * mm, "end": v(8.9, 20.3) * mm});
            skLineSegment(sketch, "E117", {"start": v(8.9, 20.3) * mm, "end": v(10, 20.3) * mm});
            skSolve(sketch);
        }
        {
            var Q0;
            Q0=makeQuery(id+"F24.imprint","IMPRINT",FACE,{"disambiguationData":[TD([[makeQuery(id+"F24.imprint","IMPRINT",EDGE,{"derivedFrom":sQuery(id+"F24.wireOp",EDGE,"E109")}),1.0]])]});
            var Q1;
            {var subQ2=sQuery(id+"F24.wireOp",EDGE,"E112");Q1=makeQuery(id+"F24.imprint","IMPRINT",FACE,{"disambiguationData":[TD([[makeQuery(id+"F24.imprint","IMPRINT",EDGE,{"derivedFrom":subQ2}),1.0]])]});}
            var Q2;
            {var subQ2=sQuery(id+"F24.wireOp",EDGE,"E117");Q2=makeQuery(id+"F24.imprint","IMPRINT",FACE,{"disambiguationData":[TD([[makeQuery(id+"F24.imprint","IMPRINT",EDGE,{"derivedFrom":subQ2}),-1.0]])]});}
            var Q3;
            {var subQ0=sQuery(id+"F24.wireOp",EDGE,"E115");Q3=makeQuery(id+"F24.imprint","IMPRINT",FACE,{"disambiguationData":[TD([[makeQuery(id+"F24.imprint","IMPRINT",EDGE,{"derivedFrom":subQ0}),1.0]])]});}
            extrude(context, id + "F25", {"entities" : qUnion([Q0, Q1, Q2, Q3]), "operationType" : NewBodyOperationType.ADD, "oppositeDirection" : true, "depth" : 2 * mm});
        }
        {
            var Q0;
            Q0=makeQuery(id+"F9.opExtrude","SWEPT_EDGE",EDGE,{"disambiguationData":[OSD([sQuery(id+"F7.wireOp",EDGE,"E81.bottom"),sQuery(id+"F7.wireOp",EDGE,"E81.left")])]});
            var Q1;
            Q1=makeQuery(id+"F9.opExtrude","SWEPT_EDGE",EDGE,{"disambiguationData":[OSD([sQuery(id+"F7.wireOp",EDGE,"E81.top"),sQuery(id+"F7.wireOp",EDGE,"E81.left")])]});
            var Q2;
            Q2=makeQuery(id+"F9.opExtrude","SWEPT_EDGE",EDGE,{"disambiguationData":[OSD([sQuery(id+"F7.wireOp",EDGE,"E81.bottom"),sQuery(id+"F7.wireOp",EDGE,"E81.right")])]});
            var Q3;
            Q3=makeQuery(id+"F9.opExtrude","SWEPT_EDGE",EDGE,{"disambiguationData":[OSD([sQuery(id+"F7.wireOp",EDGE,"E81.top"),sQuery(id+"F7.wireOp",EDGE,"E81.right")])]});
            var Q4;
            Q4=makeQuery(id+"F9.opExtrude","SWEPT_EDGE",EDGE,{"disambiguationData":[OSD([sQuery(id+"F7.wireOp",EDGE,"E82.MirrorCS"),sQuery(id+"F7.wireOp",EDGE,"E85.MirrorCS")])]});
            var Q5;
            Q5=makeQuery(id+"F9.opExtrude","SWEPT_EDGE",EDGE,{"disambiguationData":[OSD([sQuery(id+"F7.wireOp",EDGE,"E84.MirrorCS"),sQuery(id+"F7.wireOp",EDGE,"E85.MirrorCS")])]});
            var Q6;
            Q6=makeQuery(id+"F9.opExtrude","SWEPT_EDGE",EDGE,{"disambiguationData":[OSD([sQuery(id+"F7.wireOp",EDGE,"E82.MirrorCS"),sQuery(id+"F7.wireOp",EDGE,"E83.MirrorCS")])]});
            var Q7;
            Q7=makeQuery(id+"F9.opExtrude","SWEPT_EDGE",EDGE,{"disambiguationData":[OSD([sQuery(id+"F7.wireOp",EDGE,"E83.MirrorCS"),sQuery(id+"F7.wireOp",EDGE,"E84.MirrorCS")])]});
            var Q8;
            Q8=makeQuery(id+"F12.opExtrude","SWEPT_EDGE",EDGE,{"disambiguationData":[OSD([sQuery(id+"F10.wireOp",EDGE,"E93.bottom"),sQuery(id+"F10.wireOp",EDGE,"E93.right")])]});
            var Q9;
            Q9=makeQuery(id+"F12.opExtrude","SWEPT_EDGE",EDGE,{"disambiguationData":[OSD([sQuery(id+"F10.wireOp",EDGE,"E93.top"),sQuery(id+"F10.wireOp",EDGE,"E93.right")])]});
            var Q10;
            Q10=makeQuery(id+"F12.opExtrude","SWEPT_EDGE",EDGE,{"disambiguationData":[OSD([sQuery(id+"F10.wireOp",EDGE,"E95.MirrorCS"),sQuery(id+"F10.wireOp",EDGE,"E97.MirrorCS")])]});
            var Q11;
            Q11=makeQuery(id+"F12.opExtrude","SWEPT_EDGE",EDGE,{"disambiguationData":[OSD([sQuery(id+"F10.wireOp",EDGE,"E94.MirrorCS"),sQuery(id+"F10.wireOp",EDGE,"E95.MirrorCS")])]});
            var Q12;
            Q12=makeQuery(id+"F12.opExtrude","SWEPT_EDGE",EDGE,{"disambiguationData":[OSD([sQuery(id+"F10.wireOp",EDGE,"E93.bottom"),sQuery(id+"F10.wireOp",EDGE,"E93.left")])]});
            var Q13;
            Q13=makeQuery(id+"F12.opExtrude","SWEPT_EDGE",EDGE,{"disambiguationData":[OSD([sQuery(id+"F10.wireOp",EDGE,"E93.top"),sQuery(id+"F10.wireOp",EDGE,"E93.left")])]});
            var Q14;
            Q14=makeQuery(id+"F12.opExtrude","SWEPT_EDGE",EDGE,{"disambiguationData":[OSD([sQuery(id+"F10.wireOp",EDGE,"E96.MirrorCS"),sQuery(id+"F10.wireOp",EDGE,"E97.MirrorCS")])]});
            var Q15;
            Q15=makeQuery(id+"F12.opExtrude","SWEPT_EDGE",EDGE,{"disambiguationData":[OSD([sQuery(id+"F10.wireOp",EDGE,"E94.MirrorCS"),sQuery(id+"F10.wireOp",EDGE,"E96.MirrorCS")])]});
            fillet(context, id + "F26", {"entities" : qUnion([Q0, Q1, Q2, Q3, Q4, Q5, Q6, Q7, Q8, Q9, Q10, Q11, Q12, Q13, Q14, Q15]), "radius" : 1.5 * mm, "tangentPropagation" : true, "allowEdgeOverflow" : false});
        }
        {
            var Q0;
            Q0=makeQuery(id+"F12.opExtrude","CAP_FACE",FACE,{"disambiguationData":[OSD([sQuery(id+"F10.wireOp",EDGE,"E93.bottom"),sQuery(id+"F10.wireOp",EDGE,"E93.top"),sQuery(id+"F10.wireOp",EDGE,"E93.left"),sQuery(id+"F10.wireOp",EDGE,"E93.right")])],"isStart":false});
            var Q1;
            Q1=makeQuery(id+"F12.opExtrude","CAP_FACE",FACE,{"disambiguationData":[OSD([sQuery(id+"F10.wireOp",EDGE,"E94.MirrorCS"),sQuery(id+"F10.wireOp",EDGE,"E95.MirrorCS"),sQuery(id+"F10.wireOp",EDGE,"E96.MirrorCS"),sQuery(id+"F10.wireOp",EDGE,"E97.MirrorCS")])],"isStart":false});
            var Q2;
            Q2=makeQuery(id+"F9.opExtrude","CAP_FACE",FACE,{"disambiguationData":[OSD([sQuery(id+"F7.wireOp",EDGE,"E81.bottom"),sQuery(id+"F7.wireOp",EDGE,"E81.top"),sQuery(id+"F7.wireOp",EDGE,"E81.left"),sQuery(id+"F7.wireOp",EDGE,"E81.right")])],"isStart":false});
            var Q3;
            Q3=makeQuery(id+"F9.opExtrude","CAP_FACE",FACE,{"disambiguationData":[OSD([sQuery(id+"F7.wireOp",EDGE,"E82.MirrorCS"),sQuery(id+"F7.wireOp",EDGE,"E83.MirrorCS"),sQuery(id+"F7.wireOp",EDGE,"E84.MirrorCS"),sQuery(id+"F7.wireOp",EDGE,"E85.MirrorCS")])],"isStart":false});
            fillet(context, id + "F27", {"entities" : qUnion([Q0, Q1, Q2, Q3]), "radius" : 0.5 * mm, "tangentPropagation" : true, "allowEdgeOverflow" : false});
        }
        {
            var Q0;
            Q0=makeQuery(id+"F23.opExtrude","SWEPT_BODY",BODY,{"disambiguationData":[OSD([sQuery(id+"F22.wireOp",EDGE,"E105"),sQuery(id+"F22.wireOp",EDGE,"E108.top"),sQuery(id+"F22.wireOp",EDGE,"E108.left"),sQuery(id+"F22.wireOp",EDGE,"E108.right")])]});
            var Q1;
            Q1=makeQuery(id+"F23.opExtrude","SWEPT_BODY",BODY,{"disambiguationData":[OSD([sQuery(id+"F22.wireOp",EDGE,"E106"),sQuery(id+"F22.wireOp",EDGE,"E107.top"),sQuery(id+"F22.wireOp",EDGE,"E107.left"),sQuery(id+"F22.wireOp",EDGE,"E107.right")])]});
            var Q2;
            Q2=qCreatedBy(makeId("Top.planeOp"),FACE);
            mirror(context, id + "F28", {"entities" : qUnion([Q0, Q1]), "mirrorPlane" : qUnion([Q2])});
        }
        {
            var Q0;
            Q0=makeQuery(id+"F23.opExtrude","SWEPT_BODY",BODY,{"disambiguationData":[OSD([sQuery(id+"F22.wireOp",EDGE,"E105"),sQuery(id+"F22.wireOp",EDGE,"E108.top"),sQuery(id+"F22.wireOp",EDGE,"E108.left"),sQuery(id+"F22.wireOp",EDGE,"E108.right")])]});
            var Q1;
            Q1=makeQuery(id+"F23.opExtrude","SWEPT_BODY",BODY,{"disambiguationData":[OSD([sQuery(id+"F22.wireOp",EDGE,"E106"),sQuery(id+"F22.wireOp",EDGE,"E107.top"),sQuery(id+"F22.wireOp",EDGE,"E107.left"),sQuery(id+"F22.wireOp",EDGE,"E107.right")])]});
            var Q2;
            Q2=makeQuery(id+"F28.opPattern","COPY",BODY,{"derivedFrom":makeQuery(id+"F23.opExtrude","SWEPT_BODY",BODY,{"disambiguationData":[OSD([sQuery(id+"F22.wireOp",EDGE,"E105"),sQuery(id+"F22.wireOp",EDGE,"E108.top"),sQuery(id+"F22.wireOp",EDGE,"E108.left"),sQuery(id+"F22.wireOp",EDGE,"E108.right")])]}),"instanceName":"1"});
            var Q3;
            Q3=makeQuery(id+"F28.opPattern","COPY",BODY,{"derivedFrom":makeQuery(id+"F23.opExtrude","SWEPT_BODY",BODY,{"disambiguationData":[OSD([sQuery(id+"F22.wireOp",EDGE,"E106"),sQuery(id+"F22.wireOp",EDGE,"E107.top"),sQuery(id+"F22.wireOp",EDGE,"E107.left"),sQuery(id+"F22.wireOp",EDGE,"E107.right")])]}),"instanceName":"1"});
            var Q4;
            Q4=makeQuery(id+"F21.opExtrude","SWEPT_BODY",BODY,{"disambiguationData":[OSD([sQuery(id+"F20.wireOp",EDGE,"E104.bottom"),sQuery(id+"F20.wireOp",EDGE,"E104.top"),sQuery(id+"F20.wireOp",EDGE,"E104.left"),sQuery(id+"F20.wireOp",EDGE,"E104.right")])]});
            var Q5;
            Q5=makeQuery(id+"F1.opExtrude","SWEPT_BODY",BODY,{"disambiguationData":[OSD([sQuery(id+"F0.wireOp",EDGE,"E0"),sQuery(id+"F0.wireOp",EDGE,"E1"),sQuery(id+"F0.wireOp",EDGE,"E2"),sQuery(id+"F0.wireOp",EDGE,"E3"),sQuery(id+"F0.wireOp",EDGE,"E4"),sQuery(id+"F0.wireOp",EDGE,"E5"),sQuery(id+"F0.wireOp",EDGE,"E6"),sQuery(id+"F0.wireOp",EDGE,"E7"),sQuery(id+"F0.wireOp",EDGE,"E8"),sQuery(id+"F0.wireOp",EDGE,"E9"),sQuery(id+"F0.wireOp",EDGE,"E10"),sQuery(id+"F0.wireOp",EDGE,"E11"),sQuery(id+"F0.wireOp",EDGE,"E12"),sQuery(id+"F0.wireOp",EDGE,"E13"),sQuery(id+"F0.wireOp",EDGE,"E15"),sQuery(id+"F0.wireOp",EDGE,"E16"),sQuery(id+"F0.wireOp",EDGE,"E17"),sQuery(id+"F0.wireOp",EDGE,"E21"),sQuery(id+"F0.wireOp",EDGE,"E24"),sQuery(id+"F0.wireOp",EDGE,"E25"),sQuery(id+"F0.wireOp",EDGE,"E26.filletArc"),sQuery(id+"F0.wireOp",EDGE,"E27.filletArc"),sQuery(id+"F0.wireOp",EDGE,"E28.filletArc"),sQuery(id+"F0.wireOp",EDGE,"E29.filletArc"),sQuery(id+"F0.wireOp",EDGE,"E30"),sQuery(id+"F0.wireOp",EDGE,"E31.MirrorCS"),sQuery(id+"F0.wireOp",EDGE,"E32.MirrorCS"),sQuery(id+"F0.wireOp",EDGE,"E33.MirrorCS"),sQuery(id+"F0.wireOp",EDGE,"E34.MirrorCS"),sQuery(id+"F0.wireOp",EDGE,"E36.MirrorCS"),sQuery(id+"F0.wireOp",EDGE,"E37.MirrorCS"),sQuery(id+"F0.wireOp",EDGE,"E38.MirrorCS"),sQuery(id+"F0.wireOp",EDGE,"E41.MirrorCS"),sQuery(id+"F0.wireOp",EDGE,"E42.MirrorCS"),sQuery(id+"F0.wireOp",EDGE,"E43.MirrorC"),sQuery(id+"F0.wireOp",EDGE,"E44.MirrorCS"),sQuery(id+"F0.wireOp",EDGE,"E45.MirrorCS"),sQuery(id+"F0.wireOp",EDGE,"E49.MirrorCS"),sQuery(id+"F0.wireOp",EDGE,"E50.MirrorCS"),sQuery(id+"F0.wireOp",EDGE,"E51.MirrorCS"),sQuery(id+"F0.wireOp",EDGE,"E52.MirrorCS"),sQuery(id+"F0.wireOp",EDGE,"E53.MirrorCS"),sQuery(id+"F0.wireOp",EDGE,"E54.MirrorCS"),sQuery(id+"F0.wireOp",EDGE,"E55.MirrorCS"),sQuery(id+"F0.wireOp",EDGE,"E56.MirrorCS"),sQuery(id+"F0.wireOp",EDGE,"E57.MirrorCS"),sQuery(id+"F0.wireOp",EDGE,"E58.MirrorCS"),sQuery(id+"F0.wireOp",EDGE,"E60.MirrorCS"),sQuery(id+"F0.wireOp",EDGE,"E61.MirrorCS"),sQuery(id+"F0.wireOp",EDGE,"E63.MirrorCS")])]});
            booleanBodies(context, id + "F29", {"operationType" : BooleanOperationType.SUBTRACTION, "tools" : qUnion([Q0, Q1, Q2, Q3, Q4]), "targets" : qUnion([Q5])});
        }
    });
